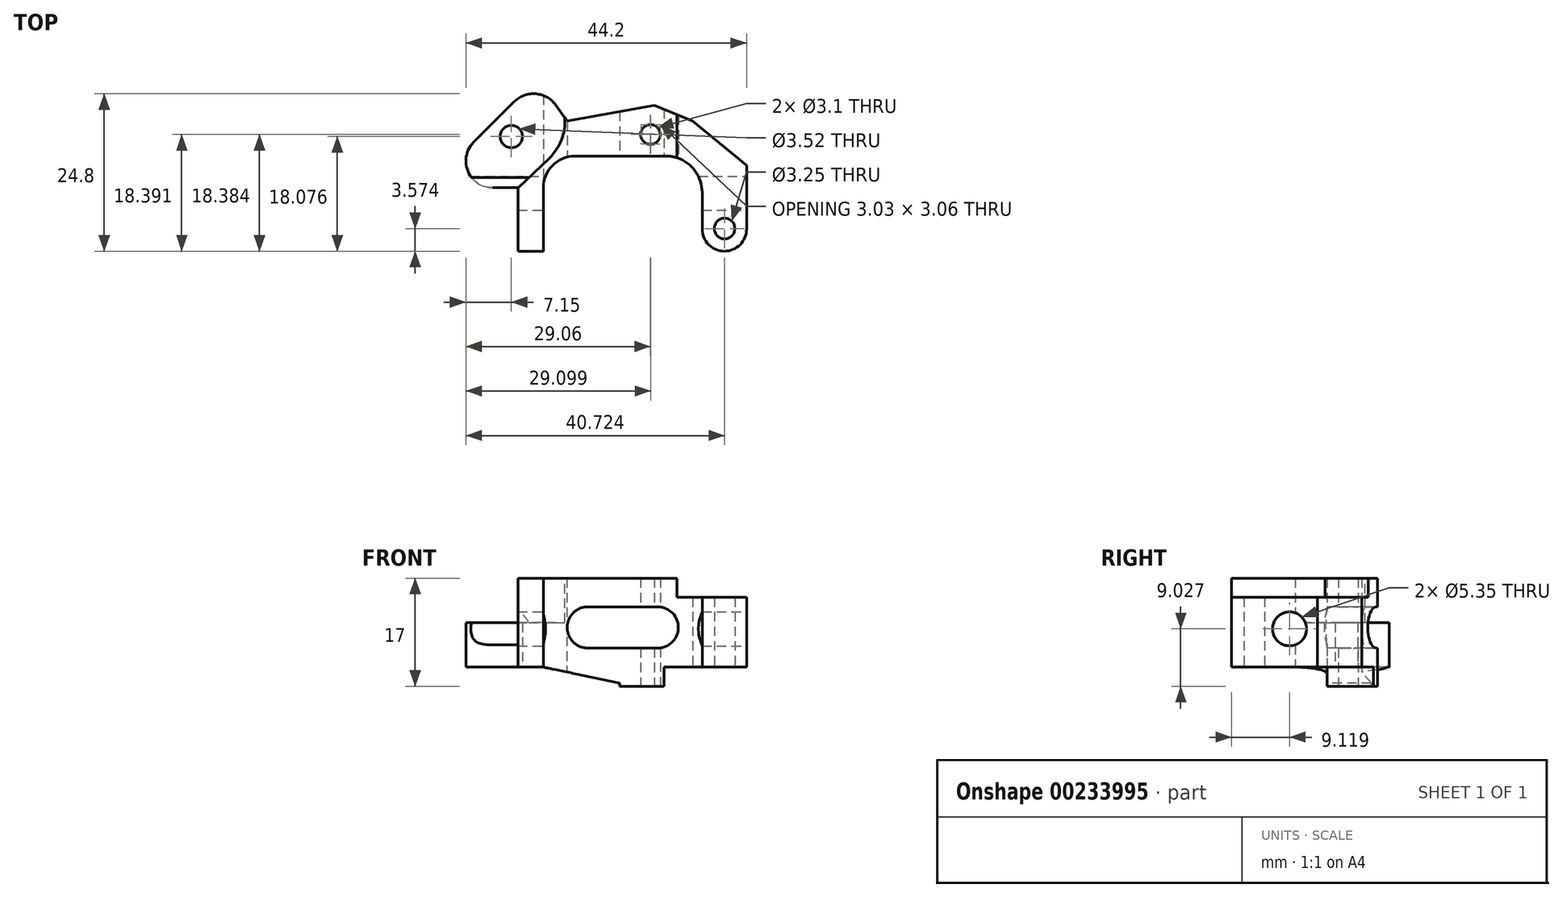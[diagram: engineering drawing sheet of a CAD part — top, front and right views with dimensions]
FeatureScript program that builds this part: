
annotation { "Feature Type Name" : "Feature", "Feature Type Description" : "" }
export const myFeature = defineFeature(function(context is Context, id is Id, definition is map)
    precondition{}
    {
        {
            var Q0;
            Q0=qCreatedBy(makeId("Top.planeOp"),FACE);
            var sketch = newSketch(context, id + "F0", { "sketchPlane" : qUnion([Q0])});
            skLineSegment(sketch, "E0", {"start": v(0, 0) * mm, "end": v(0, 15) * mm});
            skLineSegment(sketch, "E1", {"start": v(0, 15) * mm, "end": v(19.25, 15) * mm});
            skLineSegment(sketch, "E2", {"start": v(25, 9.25) * mm, "end": v(25, 3.5) * mm});
            skLineSegment(sketch, "E3", {"start": v(32, 3.5) * mm, "end": v(32, 13.5) * mm});
            skLineSegment(sketch, "E4", {"start": v(32, 13.5) * mm, "end": v(23.5, 20.48) * mm});
            skLineSegment(sketch, "E5", {"start": v(23.5, 20.48) * mm, "end": v(17.5, 22.98) * mm});
            skLineSegment(sketch, "E6", {"start": v(17.5, 22.98) * mm, "end": v(3.73, 20.48) * mm});
            skLineSegment(sketch, "E7", {"start": v(-4.6, 23.53) * mm, "end": v(-10.97, 17.17) * mm});
            skLineSegment(sketch, "E8", {"start": v(-4, 10) * mm, "end": v(-4, 0) * mm});
            skLineSegment(sketch, "E9", {"start": v(-4, 0) * mm, "end": v(0, 0) * mm});
            skArc(sketch, "E10", {"start": v(32, 3.5) * mm, "mid": v(28.5, 0) * mm, "end": v(25, 3.5) * mm});
            skPoint(sketch, "E11.orphan", {"position": v(32, 0) * mm});
            skPoint(sketch, "E12", {"position": v(28.5, 0) * mm});
            skArc(sketch, "E13", {"start": v(-10.97, 17.17) * mm, "mid": v(-11.88, 12.6) * mm, "end": v(-8, 10) * mm});
            skLineSegment(sketch, "E14", {"start": v(-8, 10) * mm, "end": v(-4, 10) * mm});
            skArc(sketch, "E15", {"start": v(-4.6, 23.53) * mm, "mid": v(-1.16, 24.79) * mm, "end": v(2.01, 22.94) * mm});
            skLineSegment(sketch, "E16", {"start": v(2.01, 22.94) * mm, "end": v(3.73, 20.48) * mm});
            skLineSegment(sketch, "E17", {"start": v(0, 0) * mm, "end": v(28.5, 0) * mm, "construction": true});
            skLineSegment(sketch, "E18", {"start": v(3.73, 20.48) * mm, "end": v(23.5, 20.48) * mm, "construction": true});
            skArc(sketch, "E19", {"start": v(25, 9.25) * mm, "mid": v(23.32, 13.32) * mm, "end": v(19.25, 15) * mm});
            skPoint(sketch, "E20.orphan", {"position": v(25, 15) * mm});
            skSolve(sketch);
        }
        {
            var Q0;
            Q0=makeQuery(id+"F0.imprint","IMPRINT",FACE,{"disambiguationData":[TD([[makeQuery(id+"F0.imprint","IMPRINT",EDGE,{"derivedFrom":sQuery(id+"F0.wireOp",EDGE,"E0")}),1.0]])]});
            extrude(context, id + "F1", {"entities" : qUnion([Q0]), "depth" : 17 * mm});
        }
        {
            var Q0;
            Q0=makeQuery(id+"F1.opExtrude","SWEPT_EDGE",EDGE,{"disambiguationData":[OSD([sQuery(id+"F0.wireOp",EDGE,"E0"),sQuery(id+"F0.wireOp",EDGE,"E1")])]});
            fillet(context, id + "F2", {"entities" : qUnion([Q0]), "radius" : 5 * mm, "tangentPropagation" : true, "allowEdgeOverflow" : false});
        }
        {
            var Q0;
            Q0=qCreatedBy(makeId("Front.planeOp"),FACE);
            var sketch = newSketch(context, id + "F3", { "sketchPlane" : qUnion([Q0])});
            skLineSegment(sketch, "E21", {"start": v(19, 0) * mm, "end": v(12, 0) * mm});
            skLineSegment(sketch, "E22", {"start": v(12, 0) * mm, "end": v(12, 0.5) * mm});
            skLineSegment(sketch, "E23", {"start": v(12, 0.5) * mm, "end": v(0, 3) * mm});
            skLineSegment(sketch, "E24", {"start": v(0, 3) * mm, "end": v(-13, 3) * mm});
            skLineSegment(sketch, "E25", {"start": v(-13, 3) * mm, "end": v(-13, 17) * mm});
            skLineSegment(sketch, "E26", {"start": v(-13, 17) * mm, "end": v(21, 17) * mm});
            skLineSegment(sketch, "E27", {"start": v(21, 17) * mm, "end": v(21, 14) * mm});
            skLineSegment(sketch, "E28", {"start": v(21, 14) * mm, "end": v(32, 14) * mm});
            skLineSegment(sketch, "E29", {"start": v(32, 14) * mm, "end": v(32, 3) * mm});
            skLineSegment(sketch, "E30", {"start": v(32, 3) * mm, "end": v(19, 3) * mm});
            skLineSegment(sketch, "E31", {"start": v(19, 3) * mm, "end": v(19, 0) * mm});
            skArc(sketch, "E32", {"start": v(7, 6) * mm, "mid": v(3.75, 9.25) * mm, "end": v(7, 12.5) * mm});
            skArc(sketch, "E33", {"start": v(18, 12.5) * mm, "mid": v(21.25, 9.25) * mm, "end": v(18, 6) * mm});
            skLineSegment(sketch, "E34", {"start": v(7, 6) * mm, "end": v(18, 6) * mm});
            skLineSegment(sketch, "E35", {"start": v(7, 12.5) * mm, "end": v(18, 12.5) * mm});
            skSolve(sketch);
        }
        {
            var Q0;
            Q0 = qSketchRegion(id + "F3", true);
            extrude(context, id + "F4", {"entities" : qUnion([Q0]), "operationType" : NewBodyOperationType.INTERSECT, "oppositeDirection" : true, "depth" : 25 * mm});
        }
        {
            var Q0;
            Q0=makeQuery(id+"F1.opExtrude","CAP_FACE",FACE,{"disambiguationData":[OSD([sQuery(id+"F0.wireOp",EDGE,"E0"),sQuery(id+"F0.wireOp",EDGE,"E1"),sQuery(id+"F0.wireOp",EDGE,"E2"),sQuery(id+"F0.wireOp",EDGE,"E3"),sQuery(id+"F0.wireOp",EDGE,"E4"),sQuery(id+"F0.wireOp",EDGE,"E5"),sQuery(id+"F0.wireOp",EDGE,"E6"),sQuery(id+"F0.wireOp",EDGE,"E7"),sQuery(id+"F0.wireOp",EDGE,"E8"),sQuery(id+"F0.wireOp",EDGE,"E9"),sQuery(id+"F0.wireOp",EDGE,"E10"),sQuery(id+"F0.wireOp",EDGE,"E13"),sQuery(id+"F0.wireOp",EDGE,"E14"),sQuery(id+"F0.wireOp",EDGE,"E15"),sQuery(id+"F0.wireOp",EDGE,"E16"),sQuery(id+"F0.wireOp",EDGE,"E19")])],"isStart":false});
            cPlane(context, id + "F5", {"entities" : qUnion([Q0]), "cplaneType" : CPlaneType.OFFSET, "offset" : 0 * mm, "width" : 150 * mm, "height" : 150 * mm});
        }
        {
            var Q0;
            Q0=qCreatedBy(id+"F5.planeOp",FACE);
            var sketch = newSketch(context, id + "F6", { "sketchPlane" : qUnion([Q0])});
            skLineSegment(sketch, "E36", {"start": v(2.53, 31.51) * mm, "end": v(-19.06, 31.51) * mm});
            skLineSegment(sketch, "E37", {"start": v(-19.06, 31.51) * mm, "end": v(-10.1, 4.18) * mm});
            skLineSegment(sketch, "E38", {"start": v(-10.1, 4.18) * mm, "end": v(0.94, 14.68) * mm});
            skArc(sketch, "E39", {"start": v(0.94, 14.68) * mm, "mid": v(3.09, 18.22) * mm, "end": v(3.16, 22.36) * mm});
            skLineSegment(sketch, "E40", {"start": v(3.16, 22.36) * mm, "end": v(2.53, 31.51) * mm});
            skSolve(sketch);
        }
        {
            var Q0;
            Q0 = qSketchRegion(id + "F6", true);
            extrude(context, id + "F7", {"entities" : qUnion([Q0]), "operationType" : NewBodyOperationType.REMOVE, "oppositeDirection" : true, "depth" : 7 * mm});
        }
        {
            var Q0;
            Q0=qCreatedBy(makeId("Top.planeOp"),FACE);
            var sketch = newSketch(context, id + "F8", { "sketchPlane" : qUnion([Q0])});
            skCircle(sketch, "E41", {"center": v(28.52, 3.57) * mm, "radius": 1.62 * mm});
            skCircle(sketch, "E42", {"center": v(16.86, 18.4) * mm, "radius": 1.55 * mm});
            skCircle(sketch, "E43", {"center": v(-5.05, 18.08) * mm, "radius": 1.76 * mm});
            skSolve(sketch);
        }
        {
            var Q0;
            Q0=qCreatedBy(makeId("Right.planeOp"),FACE);
            var sketch = newSketch(context, id + "F9", { "sketchPlane" : qUnion([Q0])});
            skCircle(sketch, "E44", {"center": v(9.12, 9.03) * mm, "radius": 2.68 * mm});
            skSolve(sketch);
        }
        {
            var Q0;
            Q0 = qSketchRegion(id + "F8", true);
            extrude(context, id + "F10", {"entities" : qUnion([Q0]), "operationType" : NewBodyOperationType.REMOVE, "depth" : 25 * mm});
        }
        {
            var Q0;
            Q0 = qSketchRegion(id + "F9", true);
            extrude(context, id + "F11", {"entities" : qUnion([Q0]), "operationType" : NewBodyOperationType.REMOVE, "endBound" : BoundingType.SYMMETRIC, "oppositeDirection" : true, "depth" : 74.6 * mm});
        }
    });
